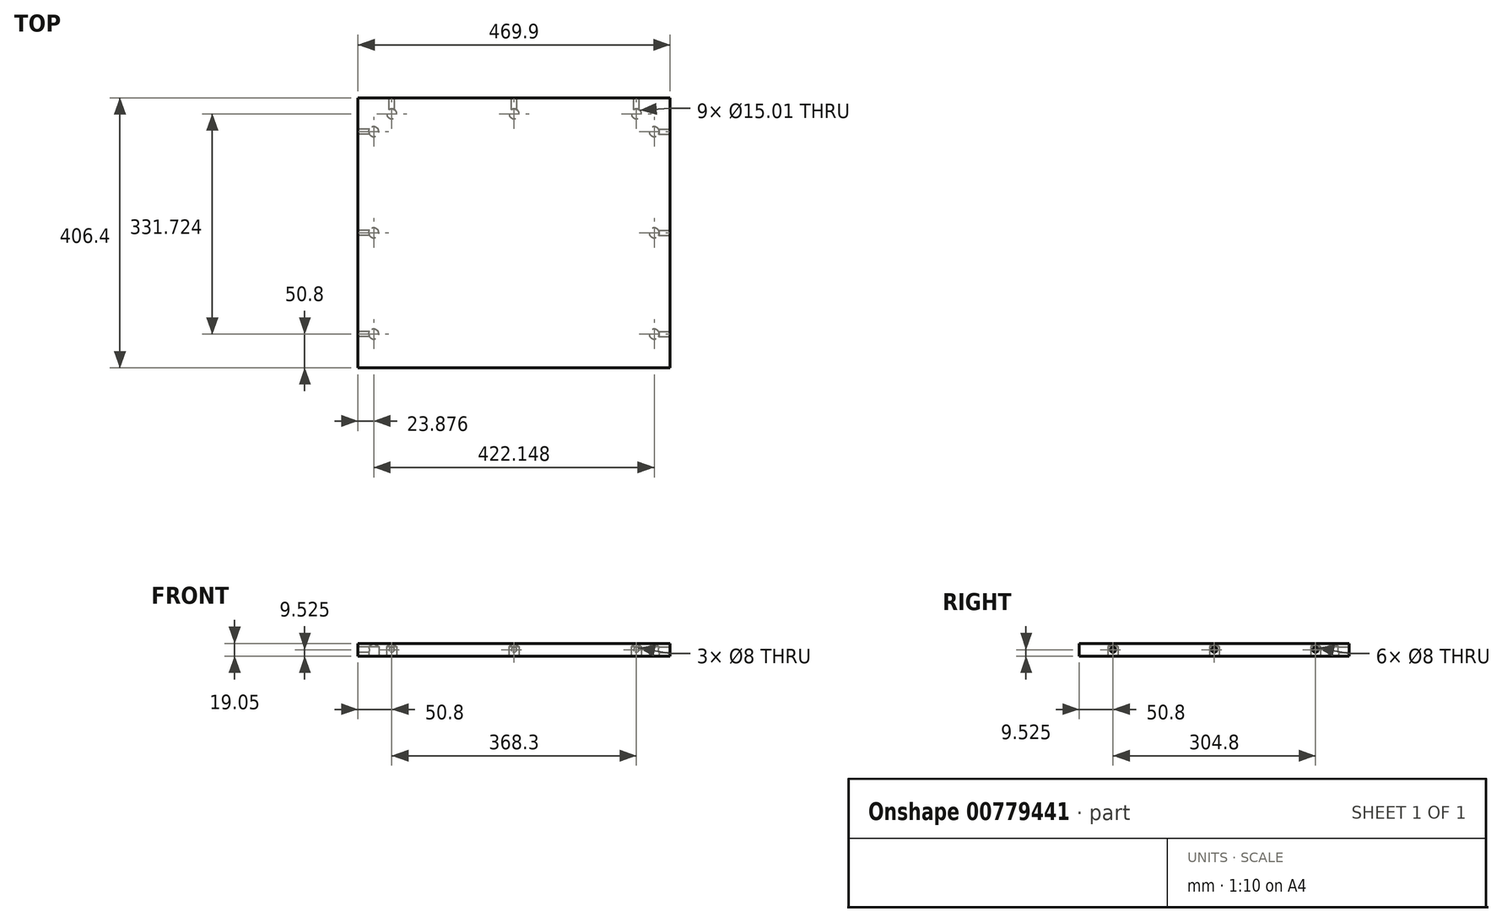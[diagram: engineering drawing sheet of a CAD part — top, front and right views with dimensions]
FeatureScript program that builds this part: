
annotation { "Feature Type Name" : "Feature", "Feature Type Description" : "" }
export const myFeature = defineFeature(function(context is Context, id is Id, definition is map)
    precondition{}
    {
        {
            var Q0;
            Q0=qCreatedBy(makeId("Top.planeOp"),FACE);
            var sketch = newSketch(context, id + "F0", { "sketchPlane" : qUnion([Q0])});
            skLineSegment(sketch, "E0.bottom", {"start": v(234.95, 203.2) * mm, "end": v(-234.95, 203.2) * mm});
            skLineSegment(sketch, "E0.top", {"start": v(234.95, -203.2) * mm, "end": v(-234.95, -203.2) * mm});
            skLineSegment(sketch, "E0.left", {"start": v(234.95, 203.2) * mm, "end": v(234.95, -203.2) * mm});
            skLineSegment(sketch, "E0.right", {"start": v(-234.95, 203.2) * mm, "end": v(-234.95, -203.2) * mm});
            skPoint(sketch, "E0.middle", {"position": v(0, 0) * mm});
            skSolve(sketch);
        }
        {
            var Q0;
            Q0=makeQuery(id+"F0.imprint","IMPRINT",FACE,{"disambiguationData":[TD([[makeQuery(id+"F0.imprint","IMPRINT",EDGE,{"derivedFrom":sQuery(id+"F0.wireOp",EDGE,"E0.bottom")}),1.0]])]});
            extrude(context, id + "F1", {"entities" : qUnion([Q0]), "depth" : 19.05 * mm, "offsetDistance" : 25.4 * mm});
        }
        {
            var Q0;
            Q0=makeQuery(id+"F1.opExtrude","CAP_FACE",FACE,{"disambiguationData":[OSD([sQuery(id+"F0.wireOp",EDGE,"E0.bottom"),sQuery(id+"F0.wireOp",EDGE,"E0.top"),sQuery(id+"F0.wireOp",EDGE,"E0.left"),sQuery(id+"F0.wireOp",EDGE,"E0.right")])],"isStart":true});
            var sketch = newSketch(context, id + "F2", { "sketchPlane" : qUnion([Q0])});
            skLineSegment(sketch, "E1", {"start": v(-234.95, 203.2) * mm, "end": v(-211.07, 203.2) * mm});
            skLineSegment(sketch, "E2", {"start": v(-211.07, 203.2) * mm, "end": v(-211.07, 152.4) * mm});
            skLineSegment(sketch, "E3", {"start": v(-234.95, -203.2) * mm, "end": v(-211.07, -203.2) * mm});
            skLineSegment(sketch, "E4", {"start": v(-211.07, -203.2) * mm, "end": v(-211.07, -152.4) * mm});
            skLineSegment(sketch, "E5", {"start": v(234.95, 203.2) * mm, "end": v(234.95, 179.32) * mm});
            skLineSegment(sketch, "E6", {"start": v(234.95, 203.2) * mm, "end": v(211.07, 203.2) * mm});
            skLineSegment(sketch, "E7", {"start": v(211.07, 203.2) * mm, "end": v(211.07, 152.4) * mm});
            skLineSegment(sketch, "E8", {"start": v(234.95, -203.2) * mm, "end": v(211.07, -203.2) * mm});
            skLineSegment(sketch, "E9", {"start": v(211.07, -203.2) * mm, "end": v(211.07, -152.4) * mm});
            skLineSegment(sketch, "E10", {"start": v(-234.95, 0) * mm, "end": v(-211.07, 0) * mm});
            skLineSegment(sketch, "E11", {"start": v(234.95, 0) * mm, "end": v(211.07, 0) * mm});
            skLineSegment(sketch, "E12", {"start": v(0, -203.2) * mm, "end": v(0, -179.32) * mm});
            skLineSegment(sketch, "E13", {"start": v(-234.95, -203.2) * mm, "end": v(-234.95, -179.32) * mm});
            skLineSegment(sketch, "E14", {"start": v(-234.95, -179.32) * mm, "end": v(-184.15, -179.32) * mm});
            skLineSegment(sketch, "E15", {"start": v(234.95, -203.2) * mm, "end": v(234.95, -179.32) * mm});
            skLineSegment(sketch, "E16", {"start": v(234.95, -179.32) * mm, "end": v(184.15, -179.32) * mm});
            skPoint(sketch, "E17", {"position": v(-211.07, 152.4) * mm});
            skPoint(sketch, "E18", {"position": v(211.07, 152.4) * mm});
            skPoint(sketch, "E19", {"position": v(211.07, 0) * mm});
            skPoint(sketch, "E20", {"position": v(-211.07, 0) * mm});
            skPoint(sketch, "E21", {"position": v(-211.07, -152.4) * mm});
            skPoint(sketch, "E22", {"position": v(-184.15, -179.32) * mm});
            skPoint(sketch, "E23", {"position": v(0, -179.32) * mm});
            skPoint(sketch, "E24", {"position": v(184.15, -179.32) * mm});
            skPoint(sketch, "E25", {"position": v(211.07, -152.4) * mm});
            skSolve(sketch);
        }
        {
            var Q0;
            Q0=sQuery(id+"F2.wireOp",VERTEX,"E17");
            var Q1;
            Q1=sQuery(id+"F2.wireOp",VERTEX,"E20");
            var Q2;
            Q2=sQuery(id+"F2.wireOp",VERTEX,"E21");
            var Q3;
            Q3=sQuery(id+"F2.wireOp",VERTEX,"E22");
            var Q4;
            Q4=sQuery(id+"F2.wireOp",VERTEX,"E23");
            var Q5;
            Q5=sQuery(id+"F2.wireOp",VERTEX,"E24");
            var Q6;
            Q6=sQuery(id+"F2.wireOp",VERTEX,"E25");
            var Q7;
            Q7=sQuery(id+"F2.wireOp",VERTEX,"E19");
            var Q8;
            Q8=sQuery(id+"F2.wireOp",VERTEX,"E18");
            var Q9;
            Q9=makeQuery(id+"F1.opExtrude","SWEPT_BODY",BODY,{"disambiguationData":[OSD([sQuery(id+"F0.wireOp",EDGE,"E0.bottom"),sQuery(id+"F0.wireOp",EDGE,"E0.top"),sQuery(id+"F0.wireOp",EDGE,"E0.left"),sQuery(id+"F0.wireOp",EDGE,"E0.right")])]});
            hole(context, id + "F3", {"style" : HoleStyle.SIMPLE, "endStyle" : HoleEndStyle.BLIND, "holeDiameter" : 15 * mm, "majorDiameter" : 6.35 * mm, "holeDepth" : 14.22 * mm, "isTappedThrough" : true, "tappedDepth" : 12.7 * mm, "tapClearance" : 3, "startFromSketch" : true, "locations" : qUnion([Q0, Q1, Q2, Q3, Q4, Q5, Q6, Q7, Q8]), "scope" : qUnion([Q9])});
        }
        {
            var Q0;
            Q0=makeQuery(id+"F1.opExtrude","SWEPT_FACE",FACE,{"disambiguationData":[OSD([sQuery(id+"F0.wireOp",EDGE,"E0.left")])]});
            var sketch = newSketch(context, id + "F4", { "sketchPlane" : qUnion([Q0])});
            skLineSegment(sketch, "E26", {"start": v(-203.2, 9.53) * mm, "end": v(-152.4, 9.53) * mm});
            skLineSegment(sketch, "E27", {"start": v(203.2, 9.53) * mm, "end": v(152.4, 9.53) * mm});
            skLineSegment(sketch, "E28", {"start": v(0, 19.05) * mm, "end": v(0, 9.53) * mm});
            skPoint(sketch, "E29", {"position": v(-152.4, 9.53) * mm});
            skPoint(sketch, "E30", {"position": v(0, 9.53) * mm});
            skPoint(sketch, "E31", {"position": v(152.4, 9.53) * mm});
            skSolve(sketch);
        }
        {
            var Q0;
            Q0=sQuery(id+"F4.wireOp",VERTEX,"E29");
            var Q1;
            Q1=sQuery(id+"F4.wireOp",VERTEX,"E30");
            var Q2;
            Q2=sQuery(id+"F4.wireOp",VERTEX,"E31");
            var Q3;
            Q3=makeQuery(id+"F1.opExtrude","SWEPT_BODY",BODY,{"disambiguationData":[OSD([sQuery(id+"F0.wireOp",EDGE,"E0.bottom"),sQuery(id+"F0.wireOp",EDGE,"E0.top"),sQuery(id+"F0.wireOp",EDGE,"E0.left"),sQuery(id+"F0.wireOp",EDGE,"E0.right")])]});
            hole(context, id + "F5", {"style" : HoleStyle.SIMPLE, "endStyle" : HoleEndStyle.BLIND, "holeDiameter" : 8 * mm, "majorDiameter" : 6.35 * mm, "holeDepth" : 25.4 * mm, "isTappedThrough" : true, "tappedDepth" : 12.7 * mm, "tapClearance" : 3, "startFromSketch" : true, "locations" : qUnion([Q0, Q1, Q2]), "scope" : qUnion([Q3])});
        }
        {
            var Q0;
            Q0=makeQuery(id+"F1.opExtrude","SWEPT_FACE",FACE,{"disambiguationData":[OSD([sQuery(id+"F0.wireOp",EDGE,"E0.bottom")])]});
            var sketch = newSketch(context, id + "F6", { "sketchPlane" : qUnion([Q0])});
            skLineSegment(sketch, "E32", {"start": v(-234.95, 9.53) * mm, "end": v(-184.15, 9.53) * mm});
            skLineSegment(sketch, "E33", {"start": v(234.95, 9.53) * mm, "end": v(184.15, 9.53) * mm});
            skLineSegment(sketch, "E34", {"start": v(0, 19.05) * mm, "end": v(0, 9.53) * mm});
            skPoint(sketch, "E35", {"position": v(-184.15, 9.53) * mm});
            skPoint(sketch, "E36", {"position": v(0, 9.53) * mm});
            skPoint(sketch, "E37", {"position": v(184.15, 9.53) * mm});
            skSolve(sketch);
        }
        {
            var Q0;
            Q0=sQuery(id+"F6.wireOp",VERTEX,"E35");
            var Q1;
            Q1=sQuery(id+"F6.wireOp",VERTEX,"E36");
            var Q2;
            Q2=sQuery(id+"F6.wireOp",VERTEX,"E37");
            var Q3;
            Q3=makeQuery(id+"F1.opExtrude","SWEPT_BODY",BODY,{"disambiguationData":[OSD([sQuery(id+"F0.wireOp",EDGE,"E0.bottom"),sQuery(id+"F0.wireOp",EDGE,"E0.top"),sQuery(id+"F0.wireOp",EDGE,"E0.left"),sQuery(id+"F0.wireOp",EDGE,"E0.right")])]});
            hole(context, id + "F7", {"style" : HoleStyle.SIMPLE, "endStyle" : HoleEndStyle.BLIND, "holeDiameter" : 8 * mm, "majorDiameter" : 6.35 * mm, "holeDepth" : 25.4 * mm, "isTappedThrough" : true, "tappedDepth" : 12.7 * mm, "tapClearance" : 3, "startFromSketch" : true, "locations" : qUnion([Q0, Q1, Q2]), "scope" : qUnion([Q3])});
        }
        {
            var Q0;
            Q0=makeQuery(id+"F1.opExtrude","SWEPT_FACE",FACE,{"disambiguationData":[OSD([sQuery(id+"F0.wireOp",EDGE,"E0.right")])]});
            var sketch = newSketch(context, id + "F8", { "sketchPlane" : qUnion([Q0])});
            skLineSegment(sketch, "E38", {"start": v(-203.2, 9.53) * mm, "end": v(-152.4, 9.53) * mm});
            skLineSegment(sketch, "E39", {"start": v(203.2, 9.53) * mm, "end": v(152.4, 9.53) * mm});
            skLineSegment(sketch, "E40", {"start": v(0, 19.05) * mm, "end": v(0, 9.53) * mm});
            skPoint(sketch, "E41", {"position": v(-152.4, 9.53) * mm});
            skPoint(sketch, "E42", {"position": v(0, 9.53) * mm});
            skPoint(sketch, "E43", {"position": v(152.4, 9.53) * mm});
            skSolve(sketch);
        }
        {
            var Q0;
            Q0=sQuery(id+"F8.wireOp",VERTEX,"E41");
            var Q1;
            Q1=sQuery(id+"F8.wireOp",VERTEX,"E42");
            var Q2;
            Q2=sQuery(id+"F8.wireOp",VERTEX,"E43");
            var Q3;
            Q3=makeQuery(id+"F1.opExtrude","SWEPT_BODY",BODY,{"disambiguationData":[OSD([sQuery(id+"F0.wireOp",EDGE,"E0.bottom"),sQuery(id+"F0.wireOp",EDGE,"E0.top"),sQuery(id+"F0.wireOp",EDGE,"E0.left"),sQuery(id+"F0.wireOp",EDGE,"E0.right")])]});
            hole(context, id + "F9", {"style" : HoleStyle.SIMPLE, "endStyle" : HoleEndStyle.BLIND, "holeDiameter" : 8 * mm, "majorDiameter" : 6.35 * mm, "holeDepth" : 25.4 * mm, "isTappedThrough" : true, "tappedDepth" : 12.7 * mm, "tapClearance" : 3, "startFromSketch" : true, "locations" : qUnion([Q0, Q1, Q2]), "scope" : qUnion([Q3])});
        }
    });
